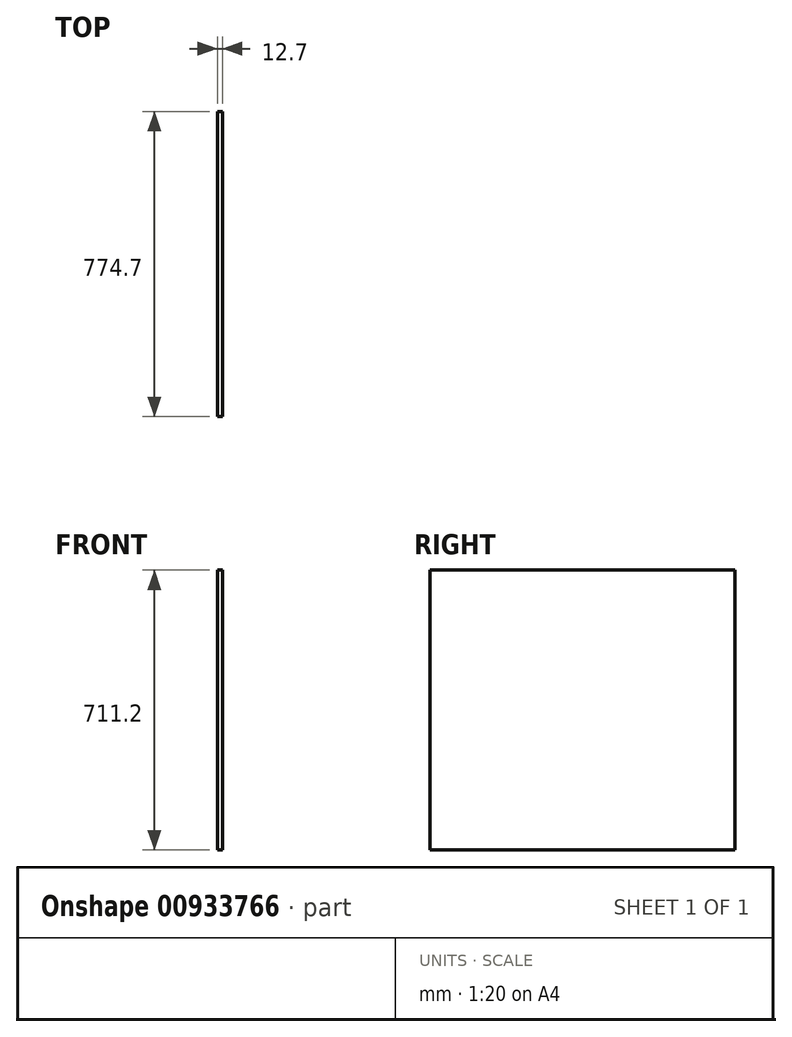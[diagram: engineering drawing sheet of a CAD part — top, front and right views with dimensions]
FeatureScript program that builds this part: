
annotation { "Feature Type Name" : "Feature", "Feature Type Description" : "" }
export const myFeature = defineFeature(function(context is Context, id is Id, definition is map)
    precondition{}
    {
        {
            var Q0;
            Q0=qCreatedBy(makeId("Right.planeOp"),FACE);
            var sketch = newSketch(context, id + "F0", { "sketchPlane" : qUnion([Q0])});
            skLineSegment(sketch, "E0.bottom", {"start": v(0, 0) * mm, "end": v(774.7, 0) * mm});
            skLineSegment(sketch, "E0.top", {"start": v(0, 711.2) * mm, "end": v(774.7, 711.2) * mm});
            skLineSegment(sketch, "E0.left", {"start": v(0, 0) * mm, "end": v(0, 711.2) * mm});
            skLineSegment(sketch, "E0.right", {"start": v(774.7, 0) * mm, "end": v(774.7, 711.2) * mm});
            skSolve(sketch);
        }
        {
            var Q0;
            Q0=makeQuery(id+"F0.imprint","IMPRINT",FACE,{"disambiguationData":[TD([[makeQuery(id+"F0.imprint","IMPRINT",EDGE,{"derivedFrom":sQuery(id+"F0.wireOp",EDGE,"E0.bottom")}),1.0]])]});
            extrude(context, id + "F1", {"entities" : qUnion([Q0]), "depth" : 12.7 * mm, "offsetDistance" : 25.4 * mm});
        }
    });
